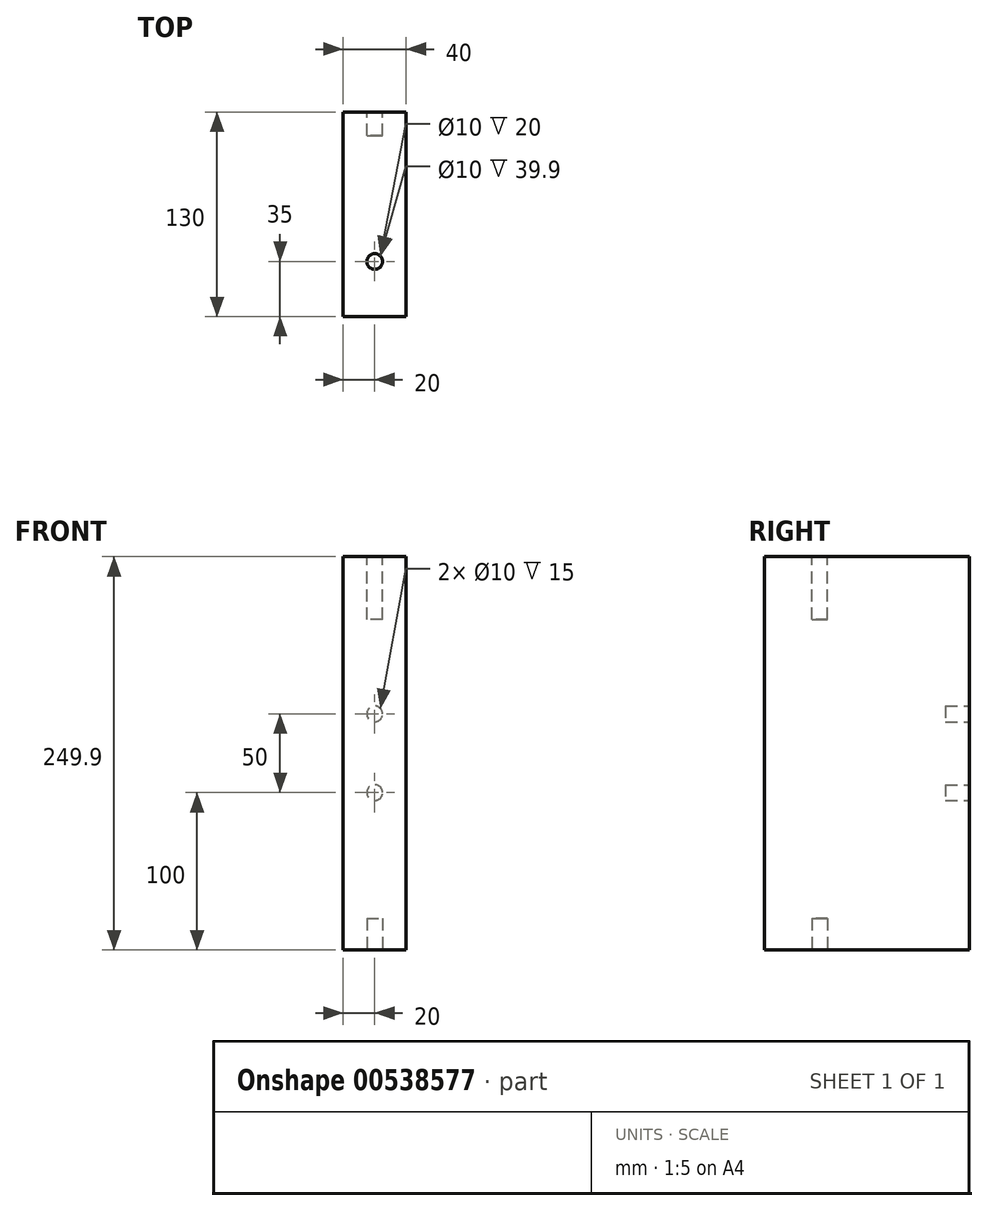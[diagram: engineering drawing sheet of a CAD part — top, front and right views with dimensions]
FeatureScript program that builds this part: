
annotation { "Feature Type Name" : "Feature", "Feature Type Description" : "" }
export const myFeature = defineFeature(function(context is Context, id is Id, definition is map)
    precondition{}
    {
        {
            var Q0;
            Q0=qCreatedBy(makeId("Top.planeOp"),FACE);
            var sketch = newSketch(context, id + "F0", { "sketchPlane" : qUnion([Q0])});
            skLineSegment(sketch, "E0.bottom", {"start": v(0, 0) * mm, "end": v(-40, 0) * mm});
            skLineSegment(sketch, "E0.top", {"start": v(0, -130) * mm, "end": v(-40, -130) * mm});
            skLineSegment(sketch, "E0.left", {"start": v(0, 0) * mm, "end": v(0, -130) * mm});
            skLineSegment(sketch, "E0.right", {"start": v(-40, 0) * mm, "end": v(-40, -130) * mm});
            skSolve(sketch);
        }
        {
            var Q0;
            Q0=makeQuery(id+"F0.imprint","IMPRINT",FACE,{"disambiguationData":[TD([[makeQuery(id+"F0.imprint","IMPRINT",EDGE,{"derivedFrom":sQuery(id+"F0.wireOp",EDGE,"E0.bottom")}),1.0]])]});
            extrude(context, id + "F1", {"entities" : qUnion([Q0]), "depth" : 250 * mm, "offsetDistance" : 25 * mm});
        }
        {
            var Q0;
            Q0=makeQuery(id+"F1.opExtrude","SWEPT_FACE",FACE,{"disambiguationData":[OSD([sQuery(id+"F0.wireOp",EDGE,"E0.bottom")])]});
            var sketch = newSketch(context, id + "F2", { "sketchPlane" : qUnion([Q0])});
            skCircle(sketch, "E1", {"center": v(20, 150) * mm, "radius": 5 * mm});
            skPoint(sketch, "E1.centerSnap0", {"position": v(20, 250) * mm});
            skCircle(sketch, "E2", {"center": v(20, 100) * mm, "radius": 5 * mm});
            skPoint(sketch, "E2.centerSnap0", {"position": v(20, 0) * mm});
            skSolve(sketch);
        }
        {
            var Q0;
            Q0=makeQuery(id+"F2.imprint","IMPRINT",FACE,{"disambiguationData":[TD([[makeQuery(id+"F2.imprint","IMPRINT",EDGE,{"derivedFrom":sQuery(id+"F2.wireOp",EDGE,"E1")}),1.0]])]});
            var Q1;
            Q1=makeQuery(id+"F2.imprint","IMPRINT",FACE,{"disambiguationData":[TD([[makeQuery(id+"F2.imprint","IMPRINT",EDGE,{"derivedFrom":sQuery(id+"F2.wireOp",EDGE,"E2")}),1.0]])]});
            extrude(context, id + "F3", {"entities" : qUnion([Q0, Q1]), "operationType" : NewBodyOperationType.REMOVE, "oppositeDirection" : true, "depth" : 15 * mm, "offsetDistance" : 25 * mm});
        }
        {
            var Q0;
            Q0=makeQuery(id+"F1.opExtrude","CAP_FACE",FACE,{"disambiguationData":[OSD([sQuery(id+"F0.wireOp",EDGE,"E0.bottom"),sQuery(id+"F0.wireOp",EDGE,"E0.top"),sQuery(id+"F0.wireOp",EDGE,"E0.left"),sQuery(id+"F0.wireOp",EDGE,"E0.right")])],"isStart":false});
            var sketch = newSketch(context, id + "F4", { "sketchPlane" : qUnion([Q0])});
            skSolve(sketch);
        }
        {
            var Q0;
            Q0=makeQuery(id+"F4.imprint","IMPRINT",FACE,{"disambiguationData":[TD([[makeQuery(id+"F4.imprint","IMPRINT",EDGE,{"derivedFrom":makeQuery(id+"F1.opExtrude","CAP_EDGE",EDGE,{"disambiguationData":[OSD([sQuery(id+"F0.wireOp",EDGE,"E0.bottom")])],"isStart":false})}),1.0]])]});
            var sketch = newSketch(context, id + "F5", { "sketchPlane" : qUnion([Q0])});
            skCircle(sketch, "E3", {"center": v(-20, -95) * mm, "radius": 5 * mm});
            skSolve(sketch);
        }
        {
            var Q0;
            Q0=makeQuery(id+"F4.imprint","IMPRINT",FACE,{"disambiguationData":[TD([[makeQuery(id+"F4.imprint","IMPRINT",EDGE,{"derivedFrom":makeQuery(id+"F1.opExtrude","CAP_EDGE",EDGE,{"disambiguationData":[OSD([sQuery(id+"F0.wireOp",EDGE,"E0.bottom")])],"isStart":false})}),1.0]])]});
            extrude(context, id + "F6", {"entities" : qUnion([Q0]), "operationType" : NewBodyOperationType.REMOVE, "oppositeDirection" : true, "depth" : 20 * mm, "offsetDistance" : 25 * mm});
        }
        {
            var Q0;
            Q0=makeQuery(id+"F5.imprint","IMPRINT",FACE,{"disambiguationData":[TD([[makeQuery(id+"F5.imprint","IMPRINT",EDGE,{"derivedFrom":sQuery(id+"F5.wireOp",EDGE,"E3")}),1.0]])]});
            extrude(context, id + "F7", {"entities" : qUnion([Q0]), "operationType" : NewBodyOperationType.REMOVE, "oppositeDirection" : true, "depth" : 40 * mm, "offsetDistance" : 25 * mm});
        }
        {
            var Q0;
            Q0=makeQuery(id+"F1.opExtrude","CAP_FACE",FACE,{"disambiguationData":[OSD([sQuery(id+"F0.wireOp",EDGE,"E0.bottom"),sQuery(id+"F0.wireOp",EDGE,"E0.top"),sQuery(id+"F0.wireOp",EDGE,"E0.left"),sQuery(id+"F0.wireOp",EDGE,"E0.right")])],"isStart":true});
            var sketch = newSketch(context, id + "F8", { "sketchPlane" : qUnion([Q0])});
            skCircle(sketch, "E4", {"center": v(-20, 95) * mm, "radius": 5 * mm});
            skSolve(sketch);
        }
        {
            var Q0;
            Q0=makeQuery(id+"F8.imprint","IMPRINT",FACE,{"disambiguationData":[TD([[makeQuery(id+"F8.imprint","IMPRINT",EDGE,{"derivedFrom":sQuery(id+"F8.wireOp",EDGE,"E4")}),1.0]])]});
            extrude(context, id + "F9", {"entities" : qUnion([Q0]), "operationType" : NewBodyOperationType.REMOVE, "oppositeDirection" : true, "depth" : 20 * mm, "offsetDistance" : 25 * mm});
        }
        {
            var Q0;
            Q0=makeQuery(id+"F6.boolean.opBoolean","COPY",FACE,{"derivedFrom":makeQuery(id+"F6.opExtrude","CAP_FACE",FACE,{"disambiguationData":[OSD([sQuery(id+"F0.wireOp",EDGE,"E0.bottom"),sQuery(id+"F0.wireOp",EDGE,"E0.top"),sQuery(id+"F0.wireOp",EDGE,"E0.left"),sQuery(id+"F0.wireOp",EDGE,"E0.right")])],"isStart":false})});
            extrude(context, id + "F10", {"entities" : qUnion([Q0]), "operationType" : NewBodyOperationType.ADD, "depth" : 19.9 * mm, "offsetDistance" : 25 * mm});
        }
    });
